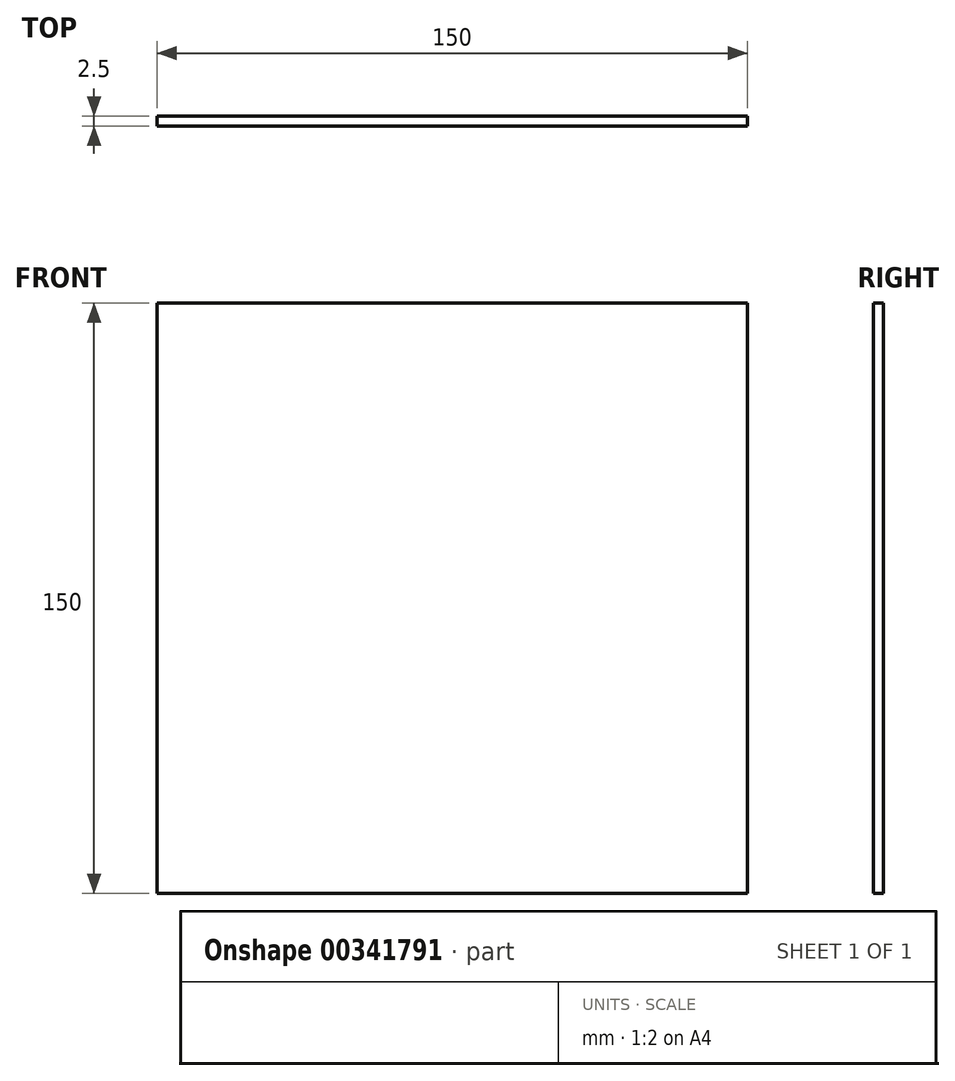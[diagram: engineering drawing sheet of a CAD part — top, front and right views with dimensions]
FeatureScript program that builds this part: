
annotation { "Feature Type Name" : "Feature", "Feature Type Description" : "" }
export const myFeature = defineFeature(function(context is Context, id is Id, definition is map)
    precondition{}
    {
        {
            var Q0;
            Q0=qCreatedBy(makeId("Front.planeOp"),FACE);
            var sketch = newSketch(context, id + "F0", { "sketchPlane" : qUnion([Q0])});
            skLineSegment(sketch, "E0.bottom", {"start": v(0, 0) * mm, "end": v(150, 0) * mm});
            skLineSegment(sketch, "E0.top", {"start": v(0, 150) * mm, "end": v(150, 150) * mm});
            skLineSegment(sketch, "E0.left", {"start": v(0, 0) * mm, "end": v(0, 150) * mm});
            skLineSegment(sketch, "E0.right", {"start": v(150, 0) * mm, "end": v(150, 150) * mm});
            skSolve(sketch);
        }
        {
            var Q0;
            Q0 = qSketchRegion(id + "F0", true);
            extrude(context, id + "F1", {"entities" : qUnion([Q0]), "depth" : 2.5 * mm});
        }
    });
